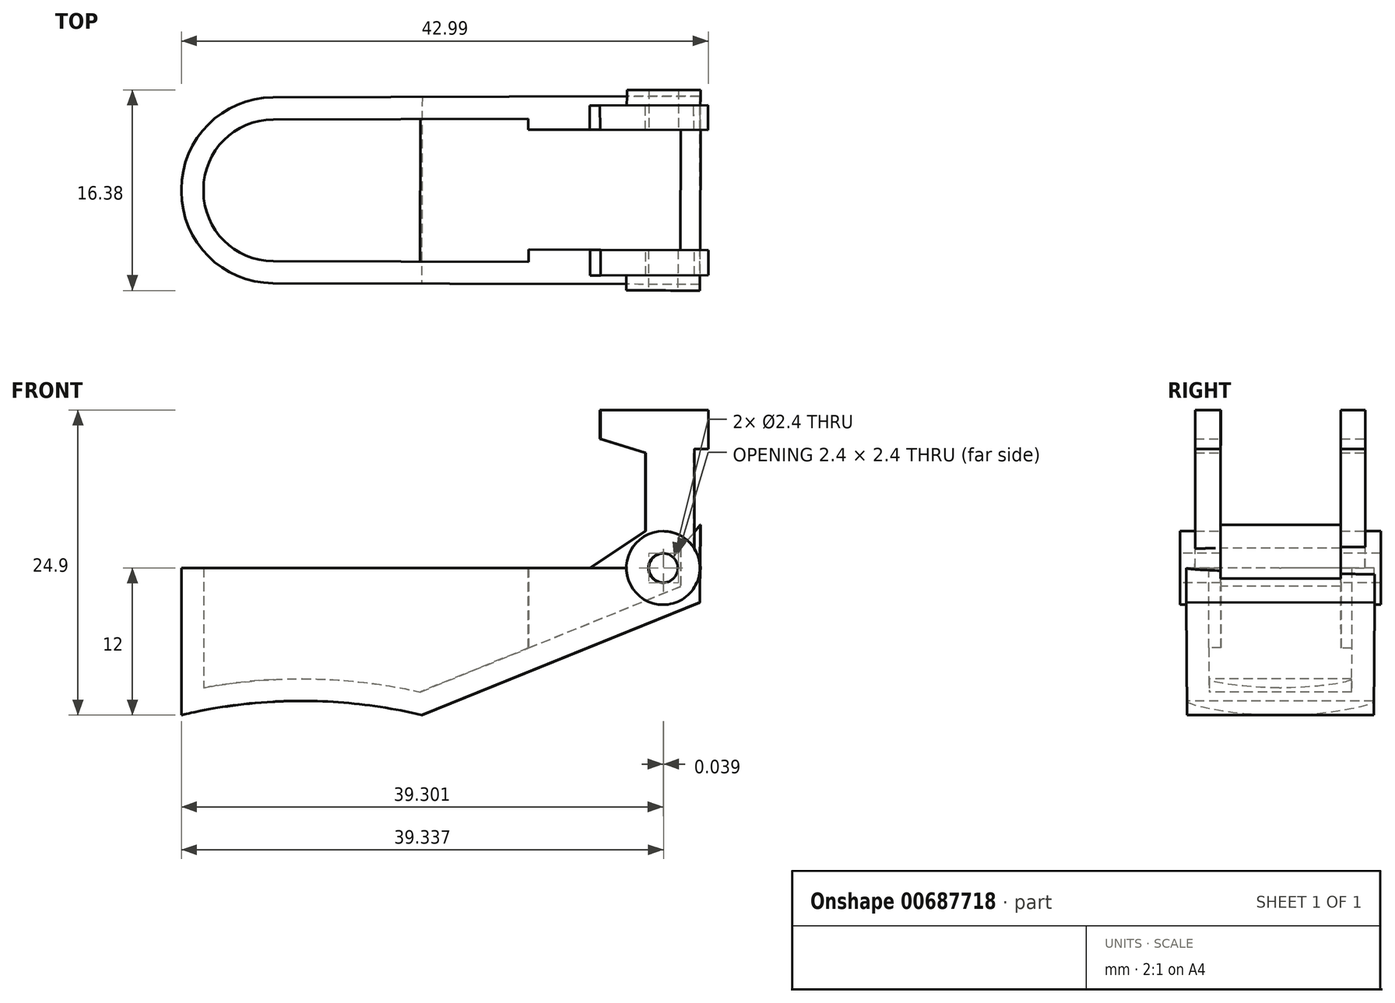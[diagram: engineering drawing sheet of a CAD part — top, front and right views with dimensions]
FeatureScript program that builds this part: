
annotation { "Feature Type Name" : "Feature", "Feature Type Description" : "" }
export const myFeature = defineFeature(function(context is Context, id is Id, definition is map)
    precondition{}
    {
        {
            var Q0;
            Q0=qCreatedBy(makeId("Top.planeOp"),FACE);
            var sketch = newSketch(context, id + "F0", { "sketchPlane" : qUnion([Q0])});
            skLineSegment(sketch, "E0.bottom", {"start": v(0, 0) * mm, "end": v(42.3, -0.13) * mm});
            skLineSegment(sketch, "E0.top", {"start": v(0, 15.12) * mm, "end": v(42.3, 15.24) * mm});
            skLineSegment(sketch, "E0.left", {"start": v(0, 0) * mm, "end": v(0, 15.12) * mm});
            skLineSegment(sketch, "E0.right", {"start": v(42.3, -0.13) * mm, "end": v(42.3, 15.24) * mm});
            skLineSegment(sketch, "E1", {"start": v(0, 7.56) * mm, "end": v(42.3, 7.56) * mm, "construction": true});
            skSolve(sketch);
        }
        {
            var Q0;
            Q0 = qSketchRegion(id + "F0", true);
            extrude(context, id + "F1", {"entities" : qUnion([Q0]), "depth" : 12 * mm, "offsetDistance" : 25 * mm});
        }
        {
            var Q0;
            Q0=makeQuery(id+"F1.opExtrude","SWEPT_FACE",FACE,{"disambiguationData":[OSD([sQuery(id+"F0.wireOp",EDGE,"E0.bottom")])]});
            var sketch = newSketch(context, id + "F2", { "sketchPlane" : qUnion([Q0])});
            skLineSegment(sketch, "E2", {"start": v(15.39, 1.15) * mm, "end": v(33.14, 1.15) * mm, "construction": true});
            skLineSegment(sketch, "E3", {"start": v(19.6, 17.8) * mm, "end": v(19.6, -10.41) * mm, "construction": true});
            skLineSegment(sketch, "E4", {"start": v(39.05, 9.2) * mm, "end": v(46.2, 9.2) * mm, "construction": true});
            skLineSegment(sketch, "E5", {"start": v(42.3, 9.2) * mm, "end": v(19.6, 0) * mm});
            skArc(sketch, "E6", {"start": v(19.6, 0) * mm, "mid": v(9.8, 1.15) * mm, "end": v(0, 0) * mm});
            skLineSegment(sketch, "E7", {"start": v(0, 0) * mm, "end": v(42.3, 0) * mm});
            skLineSegment(sketch, "E8", {"start": v(42.3, 0) * mm, "end": v(42.3, 9.2) * mm});
            skSolve(sketch);
        }
        {
            var Q0;
            Q0 = qSketchRegion(id + "F2", true);
            extrude(context, id + "F3", {"entities" : qUnion([Q0]), "operationType" : NewBodyOperationType.REMOVE, "oppositeDirection" : true, "depth" : 25 * mm, "offsetDistance" : 25 * mm});
        }
        {
            var Q0;
            Q0=makeQuery(id+"F1.opExtrude","CAP_FACE",FACE,{"disambiguationData":[OSD([sQuery(id+"F0.wireOp",EDGE,"E0.bottom"),sQuery(id+"F0.wireOp",EDGE,"E0.top"),sQuery(id+"F0.wireOp",EDGE,"E0.left"),sQuery(id+"F0.wireOp",EDGE,"E0.right")])],"isStart":false});
            shell(context, id + "F4", {"entities" : qUnion([Q0]), "thickness" : 1.8 * mm});
        }
        {
            var Q0;
            Q0=makeQuery(id+"F4.opShell","OFFSET_EDGE",EDGE,{"disambiguationData":[OSD([sQuery(id+"F0.wireOp",EDGE,"E0.top"),sQuery(id+"F0.wireOp",EDGE,"E0.left")])]});
            var Q1;
            Q1=makeQuery(id+"F4.opShell","OFFSET_EDGE",EDGE,{"disambiguationData":[OSD([sQuery(id+"F0.wireOp",EDGE,"E0.bottom"),sQuery(id+"F0.wireOp",EDGE,"E0.left")])]});
            fillet(context, id + "F5", {"entities" : qUnion([Q0, Q1]), "radius" : 5.7 * mm, "tangentPropagation" : true, "allowEdgeOverflow" : false});
        }
        {
            var Q0;
            Q0=makeQuery(id+"F1.opExtrude","SWEPT_EDGE",EDGE,{"disambiguationData":[OSD([sQuery(id+"F0.wireOp",EDGE,"E0.top"),sQuery(id+"F0.wireOp",EDGE,"E0.left")])]});
            var Q1;
            Q1=makeQuery(id+"F1.opExtrude","SWEPT_EDGE",EDGE,{"disambiguationData":[OSD([sQuery(id+"F0.wireOp",EDGE,"E0.bottom"),sQuery(id+"F0.wireOp",EDGE,"E0.left")])]});
            fillet(context, id + "F6", {"entities" : qUnion([Q0, Q1]), "radius" : 7.5 * mm, "tangentPropagation" : true, "allowEdgeOverflow" : false});
        }
        {
            var Q0;
            Q0=makeQuery(id+"F1.opExtrude","SWEPT_FACE",FACE,{"disambiguationData":[OSD([sQuery(id+"F0.wireOp",EDGE,"E0.bottom")])]});
            cPlane(context, id + "F7", {"entities" : qUnion([Q0]), "cplaneType" : CPlaneType.OFFSET, "offset" : 0.5 * mm, "width" : 150 * mm, "height" : 150 * mm});
        }
        {
            var Q0;
            Q0=qCreatedBy(id+"F7.planeOp",FACE);
            var sketch = newSketch(context, id + "F8", { "sketchPlane" : qUnion([Q0])});
            skCircle(sketch, "E9", {"center": v(39.3, 12) * mm, "radius": 3 * mm});
            skSolve(sketch);
        }
        {
            var Q0;
            Q0 = qSketchRegion(id + "F8", true);
            extrude(context, id + "F9", {"entities" : qUnion([Q0]), "operationType" : NewBodyOperationType.ADD, "oppositeDirection" : true, "depth" : 16.37 * mm, "offsetDistance" : 25 * mm});
        }
        {
            var Q0;
            Q0=makeQuery(id+"F9.opExtrude","CAP_FACE",FACE,{"disambiguationData":[OSD([sQuery(id+"F8.wireOp",EDGE,"E9")])],"isStart":true});
            var sketch = newSketch(context, id + "F10", { "sketchPlane" : qUnion([Q0])});
            skCircle(sketch, "E10", {"center": v(39.3, 12) * mm, "radius": 1.2 * mm});
            skSolve(sketch);
        }
        {
            var Q0;
            Q0 = qSketchRegion(id + "F10", true);
            extrude(context, id + "F11", {"entities" : qUnion([Q0]), "operationType" : NewBodyOperationType.REMOVE, "endBound" : BoundingType.THROUGH_ALL, "oppositeDirection" : true, "depth" : 25 * mm, "offsetDistance" : 25 * mm});
        }
        {
            var Q0;
            Q0=makeQuery(id+"F1.opExtrude","SWEPT_FACE",FACE,{"disambiguationData":[OSD([sQuery(id+"F0.wireOp",EDGE,"E0.top")])]});
            cPlane(context, id + "F12", {"entities" : qUnion([Q0]), "cplaneType" : CPlaneType.OFFSET, "offset" : 0.75 * mm, "oppositeDirection" : true, "width" : 150 * mm, "height" : 150 * mm});
        }
        {
            var Q0;
            Q0=qCreatedBy(id+"F12.planeOp",FACE);
            var sketch = newSketch(context, id + "F13", { "sketchPlane" : qUnion([Q0])});
            skLineSegment(sketch, "E11", {"start": v(-28.34, 5.2) * mm, "end": v(-39.62, 9.22) * mm});
            skLineSegment(sketch, "E12", {"start": v(-28.34, 5.2) * mm, "end": v(-28.34, 12) * mm});
            skLineSegment(sketch, "E13", {"start": v(-28.34, 12) * mm, "end": v(-33.34, 12) * mm});
            skLineSegment(sketch, "E14", {"start": v(-33.34, 12) * mm, "end": v(-37.9, 15) * mm});
            skLineSegment(sketch, "E15", {"start": v(-39.62, 9.22) * mm, "end": v(-36.94, 13.44) * mm});
            skLineSegment(sketch, "E16", {"start": v(-36.94, 13.44) * mm, "end": v(-41.84, 13.44) * mm});
            skLineSegment(sketch, "E17", {"start": v(-37.9, 15) * mm, "end": v(-37.9, 21.4) * mm});
            skLineSegment(sketch, "E18", {"start": v(-41.84, 13.44) * mm, "end": v(-41.84, 21.7) * mm});
            skLineSegment(sketch, "E19", {"start": v(-41.84, 21.7) * mm, "end": v(-43, 21.7) * mm});
            skLineSegment(sketch, "E20", {"start": v(-43, 21.7) * mm, "end": v(-43, 24.9) * mm});
            skLineSegment(sketch, "E21", {"start": v(-43, 24.9) * mm, "end": v(-34.2, 24.9) * mm});
            skLineSegment(sketch, "E22", {"start": v(-34.2, 24.9) * mm, "end": v(-34.2, 22.55) * mm});
            skLineSegment(sketch, "E23", {"start": v(-34.2, 22.55) * mm, "end": v(-37.9, 21.4) * mm});
            skSolve(sketch);
        }
        {
            var Q0;
            Q0 = qSketchRegion(id + "F13", true);
            extrude(context, id + "F14", {"entities" : qUnion([Q0]), "operationType" : NewBodyOperationType.ADD, "oppositeDirection" : true, "depth" : (15.37 - 1.5) * mm, "offsetDistance" : 25 * mm});
        }
        {
            var Q0;
            {var subQ1=sQuery(id+"F0.wireOp",EDGE,"E0.bottom");Q0=makeQuery(id+"F14.boolean.opBoolean","SPLIT",FACE,{"disambiguationData":[TD([makeQuery(id+"F4.opShell","OFFSET_FACE",FACE,{"disambiguationData":[OSD([sQuery(id+"F2.wireOp",EDGE,"E6")])]})])],"derivedFrom":makeQuery(id+"F4.opShell","OFFSET_FACE",FACE,{"disambiguationData":[OSD([subQ1])]})});}
            cPlane(context, id + "F15", {"entities" : qUnion([Q0]), "cplaneType" : CPlaneType.OFFSET, "offset" : 1 * mm, "width" : 150 * mm, "height" : 150 * mm});
        }
        {
            var Q0;
            Q0=qCreatedBy(id+"F15.planeOp",FACE);
            var sketch = newSketch(context, id + "F16", { "sketchPlane" : qUnion([Q0])});
            skLineSegment(sketch, "E24", {"start": v(-19.45, 1.88) * mm, "end": v(-45.81, 12.56) * mm});
            skLineSegment(sketch, "E25", {"start": v(-45.81, 12.56) * mm, "end": v(-45.81, 29.1) * mm});
            skLineSegment(sketch, "E26", {"start": v(-45.81, 29.1) * mm, "end": v(-19.45, 29.1) * mm});
            skLineSegment(sketch, "E27", {"start": v(-19.45, 29.1) * mm, "end": v(-19.45, 1.88) * mm});
            skSolve(sketch);
        }
        {
            var Q0;
            Q0 = qSketchRegion(id + "F16", true);
            extrude(context, id + "F17", {"entities" : qUnion([Q0]), "operationType" : NewBodyOperationType.REMOVE, "depth" : 9.8 * mm, "offsetDistance" : 25 * mm});
        }
        {
            var Q0;
            Q0=makeQuery(id+"F17.boolean.opBoolean","COPY",FACE,{"derivedFrom":makeQuery(id+"F17.opExtrude","CAP_FACE",FACE,{"disambiguationData":[OSD([sQuery(id+"F16.wireOp",EDGE,"E24"),sQuery(id+"F16.wireOp",EDGE,"E25"),sQuery(id+"F16.wireOp",EDGE,"E26"),sQuery(id+"F16.wireOp",EDGE,"E27")])],"isStart":true})});
            var sketch = newSketch(context, id + "F18", { "sketchPlane" : qUnion([Q0])});
            skLineSegment(sketch, "E28", {"start": v(-42.3, 11.14) * mm, "end": v(-42.33, 15.52) * mm});
            skLineSegment(sketch, "E29", {"start": v(-42.33, 15.52) * mm, "end": v(-40.72, 13.63) * mm});
            skLineSegment(sketch, "E30", {"start": v(-40.72, 13.63) * mm, "end": v(-40.72, 10.5) * mm});
            skLineSegment(sketch, "E31", {"start": v(-40.72, 10.5) * mm, "end": v(-42.3, 11.14) * mm});
            skSolve(sketch);
        }
        {
            var Q0;
            Q0 = qSketchRegion(id + "F18", true);
            var Q1;
            Q1=makeQuery(id+"F17.boolean.opBoolean","COPY",FACE,{"derivedFrom":makeQuery(id+"F17.opExtrude","CAP_FACE",FACE,{"disambiguationData":[OSD([sQuery(id+"F16.wireOp",EDGE,"E24"),sQuery(id+"F16.wireOp",EDGE,"E25"),sQuery(id+"F16.wireOp",EDGE,"E26"),sQuery(id+"F16.wireOp",EDGE,"E27")])],"isStart":false})});
            extrude(context, id + "F19", {"entities" : qUnion([Q0]), "operationType" : NewBodyOperationType.ADD, "endBound" : BoundingType.UP_TO_SURFACE, "depth" : 25 * mm, "endBoundEntityFace" : qUnion([Q1]), "offsetDistance" : 25 * mm});
        }
    });
